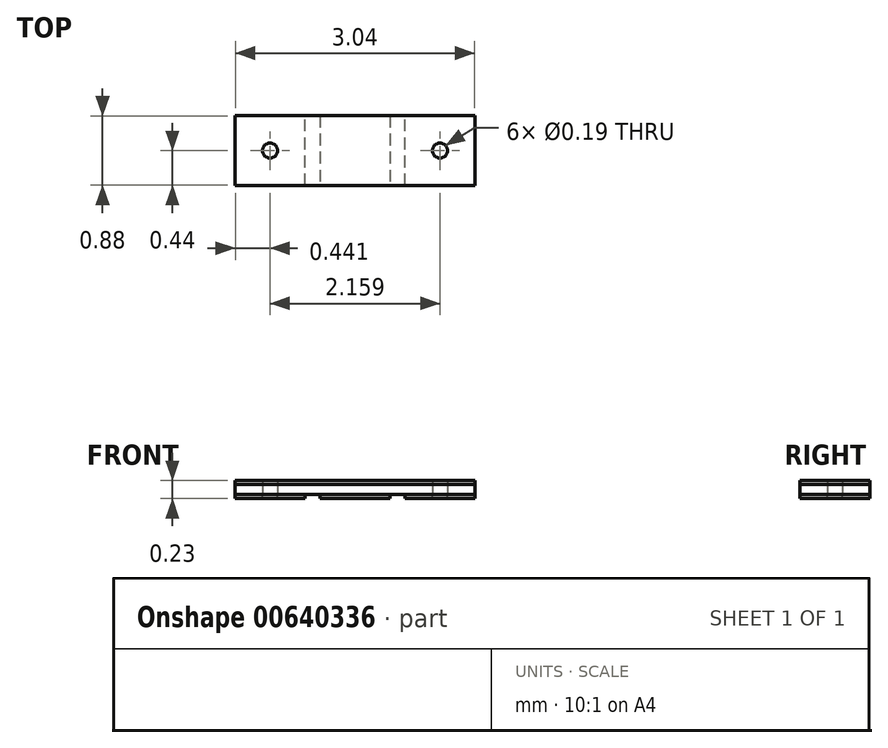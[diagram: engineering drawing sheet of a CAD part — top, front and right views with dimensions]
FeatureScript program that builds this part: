
annotation { "Feature Type Name" : "Feature", "Feature Type Description" : "" }
export const myFeature = defineFeature(function(context is Context, id is Id, definition is map)
    precondition{}
    {
        {
            var Q0;
            Q0=qCreatedBy(makeId("Top.planeOp"),FACE);
            var sketch = newSketch(context, id + "F0", { "sketchPlane" : qUnion([Q0])});
            skLineSegment(sketch, "E0.bottom", {"start": v(-1.52, -0.44) * mm, "end": v(1.52, -0.44) * mm});
            skLineSegment(sketch, "E0.top", {"start": v(-1.52, 0.44) * mm, "end": v(1.52, 0.44) * mm});
            skLineSegment(sketch, "E0.left", {"start": v(-1.52, -0.44) * mm, "end": v(-1.52, 0.44) * mm});
            skLineSegment(sketch, "E0.right", {"start": v(1.52, -0.44) * mm, "end": v(1.52, 0.44) * mm});
            skPoint(sketch, "E0.middle", {"position": v(0, 0) * mm});
            skSolve(sketch);
        }
        {
            var Q0;
            Q0=makeQuery(id+"F0.imprint","IMPRINT",FACE,{"disambiguationData":[TD([[makeQuery(id+"F0.imprint","IMPRINT",EDGE,{"derivedFrom":sQuery(id+"F0.wireOp",EDGE,"E0.bottom")}),1.0]])]});
            extrude(context, id + "F1", {"entities" : qUnion([Q0]), "depth" : 0.13 * mm, "offsetDistance" : 25.4 * mm});
        }
        {
            var Q0;
            Q0=makeQuery(id+"F1.opExtrude","CAP_FACE",FACE,{"disambiguationData":[OSD([sQuery(id+"F0.wireOp",EDGE,"E0.bottom"),sQuery(id+"F0.wireOp",EDGE,"E0.top"),sQuery(id+"F0.wireOp",EDGE,"E0.left"),sQuery(id+"F0.wireOp",EDGE,"E0.right")])],"isStart":false});
            var sketch = newSketch(context, id + "F2", { "sketchPlane" : qUnion([Q0])});
            skSolve(sketch);
        }
        {
            var Q0;
            Q0 = qSketchRegion(id + "F2", true);
            var Q1;
            Q1=makeQuery(id+"F2.imprint","IMPRINT",FACE,{"disambiguationData":[TD([[makeQuery(id+"F2.imprint","IMPRINT",EDGE,{"derivedFrom":makeQuery(id+"F1.opExtrude","CAP_EDGE",EDGE,{"disambiguationData":[OSD([sQuery(id+"F0.wireOp",EDGE,"E0.bottom")])],"isStart":false})}),1.0]])]});
            extrude(context, id + "F3", {"entities" : qUnion([Q0, Q1]), "depth" : 0.05 * mm, "offsetDistance" : 25.4 * mm});
        }
        {
            var Q0;
            Q0=makeQuery(id+"F1.opExtrude","CAP_FACE",FACE,{"disambiguationData":[OSD([sQuery(id+"F0.wireOp",EDGE,"E0.bottom"),sQuery(id+"F0.wireOp",EDGE,"E0.top"),sQuery(id+"F0.wireOp",EDGE,"E0.left"),sQuery(id+"F0.wireOp",EDGE,"E0.right")])],"isStart":true});
            var sketch = newSketch(context, id + "F4", { "sketchPlane" : qUnion([Q0])});
            skLineSegment(sketch, "E1.bottom", {"start": v(0.44, -0.44) * mm, "end": v(-0.44, -0.44) * mm});
            skLineSegment(sketch, "E1.top", {"start": v(0.44, 0.44) * mm, "end": v(-0.44, 0.44) * mm});
            skLineSegment(sketch, "E1.left", {"start": v(0.44, -0.44) * mm, "end": v(0.44, 0.44) * mm});
            skLineSegment(sketch, "E1.right", {"start": v(-0.44, -0.44) * mm, "end": v(-0.44, 0.44) * mm});
            skPoint(sketch, "E1.middle", {"position": v(0, 0) * mm});
            skCircle(sketch, "E2", {"center": v(-1.08, 0) * mm, "radius": 0.1 * mm});
            skLineSegment(sketch, "E3.0", {"start": v(-1.52, 0.44) * mm, "end": v(-1.52, -0.44) * mm});
            skLineSegment(sketch, "E4", {"start": v(-1.08, 0.44) * mm, "end": v(-1.08, -0.44) * mm, "construction": true});
            skLineSegment(sketch, "E5.MirrorCS", {"start": v(-0.64, 0.44) * mm, "end": v(-0.64, -0.44) * mm});
            skLineSegment(sketch, "E6", {"start": v(-1.52, 0.44) * mm, "end": v(-0.64, 0.44) * mm});
            skLineSegment(sketch, "E7", {"start": v(-1.52, -0.44) * mm, "end": v(-0.64, -0.44) * mm});
            skLineSegment(sketch, "E8.MirrorCS", {"start": v(0.64, 0.44) * mm, "end": v(0.64, -0.44) * mm});
            skLineSegment(sketch, "E9.MirrorCS", {"start": v(1.52, 0.44) * mm, "end": v(0.64, 0.44) * mm});
            skLineSegment(sketch, "E10.MirrorCS", {"start": v(1.52, 0.44) * mm, "end": v(1.52, -0.44) * mm});
            skLineSegment(sketch, "E11.MirrorCS", {"start": v(1.52, -0.44) * mm, "end": v(0.64, -0.44) * mm});
            skCircle(sketch, "E12.MirrorC", {"center": v(1.08, 0) * mm, "radius": 0.1 * mm});
            skSolve(sketch);
        }
        {
            var Q0;
            Q0=makeQuery(id+"F4.imprint","IMPRINT",FACE,{"disambiguationData":[TD([[makeQuery(id+"F4.imprint","IMPRINT",EDGE,{"derivedFrom":sQuery(id+"F4.wireOp",EDGE,"E2")}),-1.0]])]});
            var Q1;
            Q1=makeQuery(id+"F4.imprint","IMPRINT",FACE,{"disambiguationData":[TD([[makeQuery(id+"F4.imprint","IMPRINT",EDGE,{"derivedFrom":sQuery(id+"F4.wireOp",EDGE,"E1.bottom")}),1.0]])]});
            var Q2;
            Q2=makeQuery(id+"F4.imprint","IMPRINT",FACE,{"disambiguationData":[TD([[makeQuery(id+"F4.imprint","IMPRINT",EDGE,{"derivedFrom":sQuery(id+"F4.wireOp",EDGE,"E8.MirrorCS")}),1.0]])]});
            extrude(context, id + "F5", {"entities" : qUnion([Q0, Q1, Q2]), "depth" : 0.05 * mm, "offsetDistance" : 25.4 * mm});
        }
        {
            var Q0;
            Q0=makeQuery(id+"F1.opExtrude","CAP_FACE",FACE,{"disambiguationData":[OSD([sQuery(id+"F0.wireOp",EDGE,"E0.bottom"),sQuery(id+"F0.wireOp",EDGE,"E0.top"),sQuery(id+"F0.wireOp",EDGE,"E0.left"),sQuery(id+"F0.wireOp",EDGE,"E0.right")])],"isStart":true});
            var sketch = newSketch(context, id + "F6", { "sketchPlane" : qUnion([Q0])});
            skCircle(sketch, "E13.0", {"center": v(-1.08, 0) * mm, "radius": 0.1 * mm});
            skCircle(sketch, "E14.0", {"center": v(1.08, 0) * mm, "radius": 0.1 * mm});
            skSolve(sketch);
        }
        {
            var Q0;
            Q0=makeQuery(id+"F6.imprint","IMPRINT",FACE,{"disambiguationData":[TD([[makeQuery(id+"F6.imprint","IMPRINT",EDGE,{"derivedFrom":sQuery(id+"F6.wireOp",EDGE,"E13.0")}),1.0]])]});
            var Q1;
            Q1=makeQuery(id+"F6.imprint","IMPRINT",FACE,{"disambiguationData":[TD([[makeQuery(id+"F6.imprint","IMPRINT",EDGE,{"derivedFrom":sQuery(id+"F6.wireOp",EDGE,"E14.0")}),1.0]])]});
            extrude(context, id + "F7", {"entities" : qUnion([Q0, Q1]), "operationType" : NewBodyOperationType.REMOVE, "endBound" : BoundingType.THROUGH_ALL, "oppositeDirection" : true, "depth" : 25.4 * mm, "offsetDistance" : 25.4 * mm});
        }
    });
